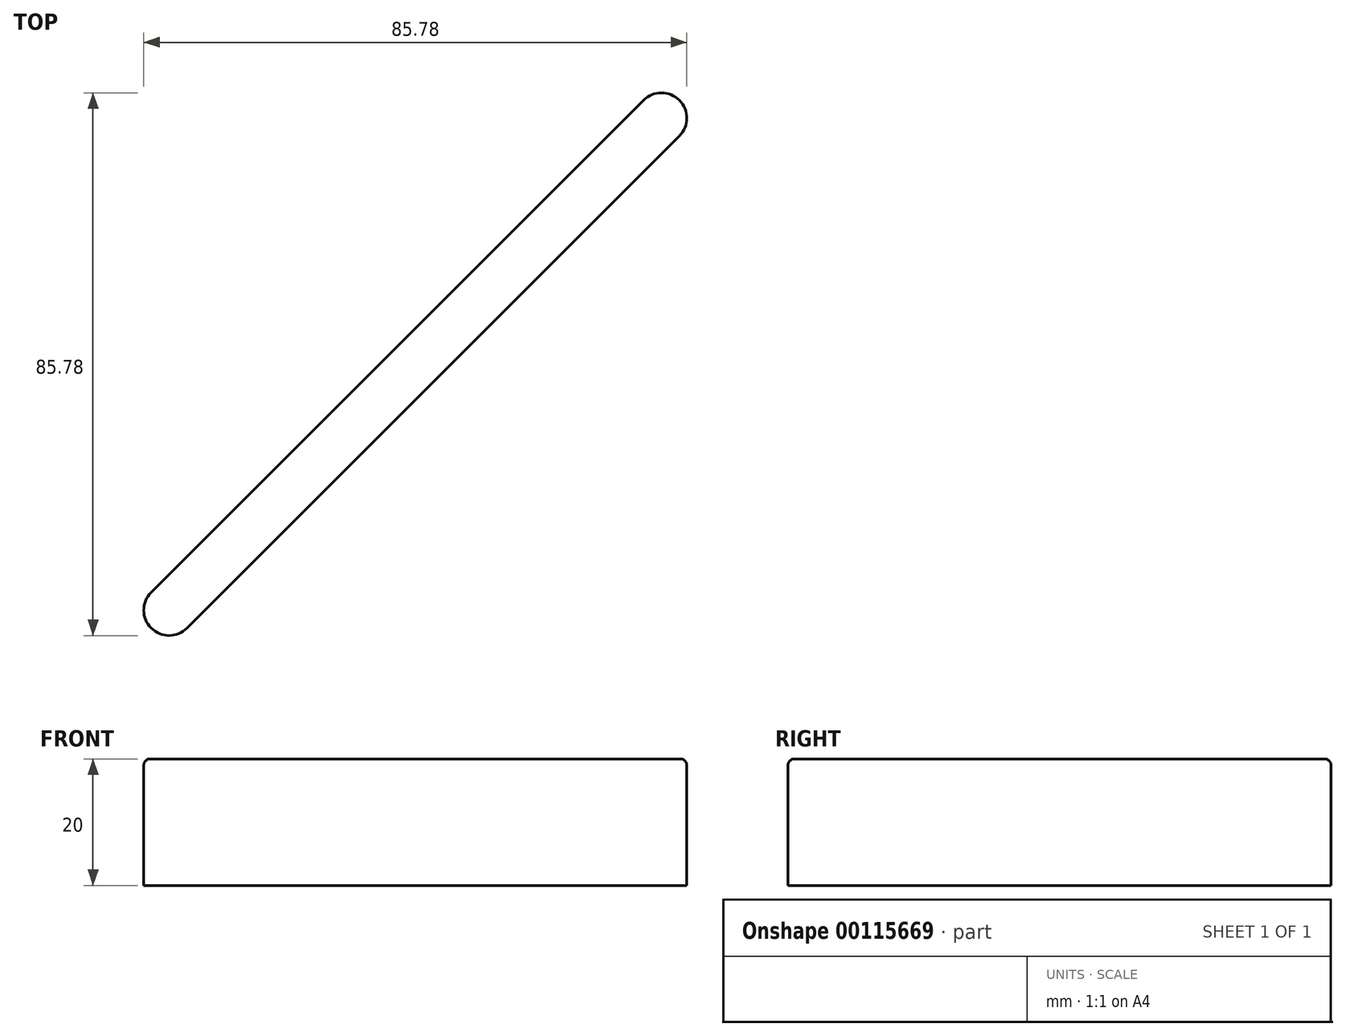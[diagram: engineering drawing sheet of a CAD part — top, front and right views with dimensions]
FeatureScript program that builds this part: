
annotation { "Feature Type Name" : "Feature", "Feature Type Description" : "" }
export const myFeature = defineFeature(function(context is Context, id is Id, definition is map)
    precondition{}
    {
        {
            var Q0;
            Q0=qCreatedBy(makeId("Top.planeOp"),FACE);
            var sketch = newSketch(context, id + "F0", { "sketchPlane" : qUnion([Q0])});
            skLineSegment(sketch, "E0.bottom", {"start": v(15.15, 65.55) * mm, "end": v(85.15, 65.55) * mm});
            skLineSegment(sketch, "E0.top", {"start": v(15.15, 58.55) * mm, "end": v(85.15, 58.55) * mm});
            skLineSegment(sketch, "E0.left", {"start": v(15.15, 65.55) * mm, "end": v(15.15, 58.55) * mm});
            skLineSegment(sketch, "E0.right", {"start": v(85.15, 65.55) * mm, "end": v(85.15, 58.55) * mm});
            skLineSegment(sketch, "E1", {"start": v(-34.78, -47.52) * mm, "end": v(71.3, 58.55) * mm});
            skLineSegment(sketch, "E2", {"start": v(71.3, 58.55) * mm, "end": v(43, 58.55) * mm});
            skLineSegment(sketch, "E3", {"start": v(43, 58.55) * mm, "end": v(-34.78, -19.23) * mm});
            skPoint(sketch, "E4", {"position": v(57.15, 58.55) * mm});
            skPoint(sketch, "E5", {"position": v(15.15, 58.55) * mm});
            skLineSegment(sketch, "E6", {"start": v(-34.78, -47.52) * mm, "end": v(-34.78, -19.23) * mm});
            skLineSegment(sketch, "E7", {"start": v(-34.78, 8.62) * mm, "end": v(-34.78, -61.38) * mm});
            skLineSegment(sketch, "E8", {"start": v(-34.78, -61.38) * mm, "end": v(-41.78, -61.38) * mm});
            skLineSegment(sketch, "E9", {"start": v(-34.78, 8.62) * mm, "end": v(-41.78, 8.62) * mm});
            skLineSegment(sketch, "E10", {"start": v(-41.78, -61.38) * mm, "end": v(-41.78, 8.62) * mm});
            skPoint(sketch, "E11", {"position": v(-34.78, -33.38) * mm});
            skLineSegment(sketch, "E12", {"start": v(-34.78, -19.23) * mm, "end": v(-20.63, -33.38) * mm, "construction": true});
            skLineSegment(sketch, "E13", {"start": v(43, 58.55) * mm, "end": v(57.15, 44.4) * mm, "construction": true});
            skPoint(sketch, "E14", {"position": v(50.08, 51.48) * mm});
            skPoint(sketch, "E15", {"position": v(-27.7, -26.3) * mm});
            skLineSegment(sketch, "E16", {"start": v(77.5, 78.9) * mm, "end": v(-73.08, -71.68) * mm, "construction": true});
            skSolve(sketch);
        }
        {
            var Q0;
            Q0=makeQuery(id+"F0.imprint","IMPRINT",FACE,{"disambiguationData":[TD([[makeQuery(id+"F0.imprint","IMPRINT",EDGE,{"derivedFrom":sQuery(id+"F0.wireOp",EDGE,"73e61f8d-8661-40f2-8c05-ec82681df63f.top")}),1.0]])]});
            var Q1;
            {var subQ0=sQuery(id+"F0.wireOp",EDGE,"E1");Q1=makeQuery(id+"F0.imprint","IMPRINT",FACE,{"disambiguationData":[TD([[makeQuery(id+"F0.imprint","IMPRINT",EDGE,{"derivedFrom":subQ0}),1.0]])]});}
            var Q2;
            Q2=makeQuery(id+"F0.imprint","IMPRINT",FACE,{"disambiguationData":[TD([[makeQuery(id+"F0.imprint","IMPRINT",EDGE,{"derivedFrom":sQuery(id+"F0.wireOp",EDGE,"E0.bottom")}),-1.0]])]});
            var Q3;
            {var subQ0=sQuery(id+"F0.wireOp",EDGE,"E8");Q3=makeQuery(id+"F0.imprint","IMPRINT",FACE,{"disambiguationData":[TD([[makeQuery(id+"F0.imprint","IMPRINT",EDGE,{"derivedFrom":subQ0}),-1.0]])]});}
            extrude(context, id + "F1", {"entities" : qUnion([Q0, Q1, Q2, Q3]), "oppositeDirection" : true, "depth" : 20 * mm});
        }
        {
            var Q0;
            {var subQ0=sQuery(id+"F0.wireOp",EDGE,"E0.top");Q0=makeQuery(id+"F1.opExtrude","SWEPT_FACE",FACE,{"disambiguationData":[OSD([subQ0]),TDD([makeQuery(id+"F0.imprint","IMPRINT",EDGE,{"disambiguationData":[TD([[makeQuery(id+"F0.imprint","INTERSECT",VERTEX,{"derivedFrom":[subQ0,sQuery(id+"F0.wireOp",EDGE,"E0.right")]}),1.0]])],"derivedFrom":subQ0})])]});}
            var sketch = newSketch(context, id + "F2", { "sketchPlane" : qUnion([Q0])});
            skPoint(sketch, "E17", {"position": v(78.22, 0) * mm});
            skPoint(sketch, "E18", {"position": v(85.15, -10) * mm});
            skPoint(sketch, "E19", {"position": v(78.22, -10) * mm});
            skSolve(sketch);
        }
        {
            var Q0;
            {var subQ0=sQuery(id+"F0.wireOp",EDGE,"E7");Q0=makeQuery(id+"F1.opExtrude","SWEPT_FACE",FACE,{"disambiguationData":[OSD([subQ0]),TDD([makeQuery(id+"F0.imprint","IMPRINT",EDGE,{"disambiguationData":[TD([[makeQuery(id+"F0.imprint","INTERSECT",VERTEX,{"derivedFrom":[sQuery(id+"F0.wireOp",EDGE,"E1"),subQ0]}),-1.0]])],"derivedFrom":subQ0})])]});}
            var sketch = newSketch(context, id + "F3", { "sketchPlane" : qUnion([Q0])});
            skPoint(sketch, "E20", {"position": v(-61.38, 0) * mm});
            skPoint(sketch, "E21", {"position": v(-54.45, 0) * mm});
            skPoint(sketch, "E22", {"position": v(-61.38, -10) * mm});
            skPoint(sketch, "E23", {"position": v(-54.45, -10) * mm});
            skSolve(sketch);
        }
        {
            var Q0;
            {var subQ0=sQuery(id+"F0.wireOp",EDGE,"E0.top");Q0=makeQuery(id+"F1.opExtrude","SWEPT_FACE",FACE,{"disambiguationData":[OSD([subQ0]),TDD([makeQuery(id+"F0.imprint","IMPRINT",EDGE,{"disambiguationData":[TD([[makeQuery(id+"F0.imprint","INTERSECT",VERTEX,{"derivedFrom":[subQ0,sQuery(id+"F0.wireOp",EDGE,"E0.left")]}),-1.0]])],"derivedFrom":subQ0})])]});}
            var sketch = newSketch(context, id + "F4", { "sketchPlane" : qUnion([Q0])});
            skPoint(sketch, "E24", {"position": v(15.15, -10) * mm});
            skPoint(sketch, "E25", {"position": v(22.08, 0) * mm});
            skPoint(sketch, "E26", {"position": v(22.08, -10) * mm});
            skSolve(sketch);
        }
        {
            var Q0;
            {var subQ0=sQuery(id+"F0.wireOp",EDGE,"E7");Q0=makeQuery(id+"F1.opExtrude","SWEPT_FACE",FACE,{"disambiguationData":[OSD([subQ0]),TDD([makeQuery(id+"F0.imprint","IMPRINT",EDGE,{"disambiguationData":[TD([[makeQuery(id+"F0.imprint","INTERSECT",VERTEX,{"derivedFrom":[sQuery(id+"F0.wireOp",EDGE,"E3"),subQ0]}),1.0]])],"derivedFrom":subQ0})])]});}
            var sketch = newSketch(context, id + "F5", { "sketchPlane" : qUnion([Q0])});
            skPoint(sketch, "E27", {"position": v(8.62, -20) * mm});
            skPoint(sketch, "E28", {"position": v(8.62, -10) * mm});
            skPoint(sketch, "E29", {"position": v(1.7, -20) * mm});
            skPoint(sketch, "E30", {"position": v(1.7, -10) * mm});
            skSolve(sketch);
        }
        {
            var Q0;
            Q0=sQuery(id+"F5.wireOp",VERTEX,"E30");
            var Q1;
            Q1=sQuery(id+"F3.wireOp",VERTEX,"E23");
            var Q2;
            Q2=sQuery(id+"F4.wireOp",VERTEX,"E26");
            var Q3;
            Q3=sQuery(id+"F2.wireOp",VERTEX,"E19");
            var Q4;
            Q4=makeQuery(id+"F1.opExtrude","SWEPT_BODY",BODY,{"disambiguationData":[OSD([sQuery(id+"F0.wireOp",EDGE,"E0.bottom"),sQuery(id+"F0.wireOp",EDGE,"E0.top"),sQuery(id+"F0.wireOp",EDGE,"E0.left"),sQuery(id+"F0.wireOp",EDGE,"E0.right"),sQuery(id+"F0.wireOp",EDGE,"E1"),sQuery(id+"F0.wireOp",EDGE,"E3"),sQuery(id+"F0.wireOp",EDGE,"E7"),sQuery(id+"F0.wireOp",EDGE,"E8"),sQuery(id+"F0.wireOp",EDGE,"E9"),sQuery(id+"F0.wireOp",EDGE,"E10")])]});
            hole(context, id + "F6", {"style" : HoleStyle.SIMPLE, "endStyle" : HoleEndStyle.THROUGH, "standardTappedOrClearance" : lookupTablePath({ "standard" : "ISO", "fit" : "Normal", "size" : "M5", "type" : "Clearance" }), "standardBlindInLast" : lookupTablePath({ "fit" : "Standard", "standard" : "ISO", "size" : "M5", "type" : "Clearance" }), "holeDiameter" : 5.5 * mm, "locations" : qUnion([Q0, Q1, Q2, Q3]), "scope" : qUnion([Q4]), "isTappedThrough" : true});
        }
        {
            var Q0;
            Q0=makeQuery(id+"F1.opExtrude","SWEPT_EDGE",EDGE,{"disambiguationData":[OSD([sQuery(id+"F0.wireOp",EDGE,"E1"),sQuery(id+"F0.wireOp",EDGE,"E7")])]});
            var Q1;
            Q1=makeQuery(id+"F1.opExtrude","SWEPT_EDGE",EDGE,{"disambiguationData":[OSD([sQuery(id+"F0.wireOp",EDGE,"E0.top"),sQuery(id+"F0.wireOp",EDGE,"E1"),sQuery(id+"F0.wireOp",EDGE,"E2")])]});
            fillet(context, id + "F7", {"entities" : qUnion([Q0, Q1]), "radius" : 5 * mm, "tangentPropagation" : true, "allowEdgeOverflow" : false});
        }
        {
            var Q0;
            Q0=makeQuery(id+"F1.opExtrude","SWEPT_EDGE",EDGE,{"disambiguationData":[OSD([sQuery(id+"F0.wireOp",EDGE,"E3"),sQuery(id+"F0.wireOp",EDGE,"E7")])]});
            var Q1;
            Q1=makeQuery(id+"F1.opExtrude","SWEPT_EDGE",EDGE,{"disambiguationData":[OSD([sQuery(id+"F0.wireOp",EDGE,"E0.top"),sQuery(id+"F0.wireOp",EDGE,"E2"),sQuery(id+"F0.wireOp",EDGE,"E3")])]});
            fillet(context, id + "F8", {"entities" : qUnion([Q0, Q1]), "radius" : 5 * mm, "tangentPropagation" : true, "allowEdgeOverflow" : false});
        }
        {
            var Q0;
            Q0=makeQuery(id+"F1.opExtrude","CAP_FACE",FACE,{"disambiguationData":[OSD([sQuery(id+"F0.wireOp",EDGE,"E0.bottom"),sQuery(id+"F0.wireOp",EDGE,"E0.top"),sQuery(id+"F0.wireOp",EDGE,"E0.left"),sQuery(id+"F0.wireOp",EDGE,"E0.right"),sQuery(id+"F0.wireOp",EDGE,"E1"),sQuery(id+"F0.wireOp",EDGE,"E3"),sQuery(id+"F0.wireOp",EDGE,"E7"),sQuery(id+"F0.wireOp",EDGE,"E8"),sQuery(id+"F0.wireOp",EDGE,"E9"),sQuery(id+"F0.wireOp",EDGE,"E10")])],"isStart":false});
            var sketch = newSketch(context, id + "F9", { "sketchPlane" : qUnion([Q0])});
            skLineSegment(sketch, "E31", {"start": v(50.08, -51.48) * mm, "end": v(-27.7, 26.3) * mm});
            skArc(sketch, "E32.0.startCap", {"start": v(52.9, -48.65) * mm, "mid": v(52.9, -54.3) * mm, "end": v(47.25, -54.3) * mm});
            skArc(sketch, "E32.0.endCap", {"start": v(-30.53, 23.48) * mm, "mid": v(-30.53, 29.13) * mm, "end": v(-24.88, 29.13) * mm});
            skLineSegment(sketch, "E32.0.left", {"start": v(47.25, -54.3) * mm, "end": v(-30.53, 23.48) * mm});
            skLineSegment(sketch, "E32.0.right", {"start": v(52.9, -48.65) * mm, "end": v(-24.88, 29.13) * mm});
            skSolve(sketch);
        }
        {
            var Q0;
            Q0=makeQuery(id+"F9.imprint","IMPRINT",FACE,{"disambiguationData":[TD([[makeQuery(id+"F9.imprint","IMPRINT",EDGE,{"derivedFrom":sQuery(id+"F9.wireOp",EDGE,"E32.0.startCap")}),-1.0]])]});
            extrude(context, id + "F10", {"entities" : qUnion([Q0]), "operationType" : NewBodyOperationType.REMOVE, "endBound" : BoundingType.THROUGH_ALL, "oppositeDirection" : true, "depth" : 25 * mm});
        }
        {
            var Q0;
            Q0=makeQuery(id+"F1.opExtrude","SWEPT_EDGE",EDGE,{"disambiguationData":[OSD([sQuery(id+"F0.wireOp",EDGE,"E0.top"),sQuery(id+"F0.wireOp",EDGE,"E0.right")])]});
            var Q1;
            Q1=makeQuery(id+"F1.opExtrude","SWEPT_EDGE",EDGE,{"disambiguationData":[OSD([sQuery(id+"F0.wireOp",EDGE,"E0.top"),sQuery(id+"F0.wireOp",EDGE,"E0.left")])]});
            var Q2;
            Q2=makeQuery(id+"F1.opExtrude","SWEPT_EDGE",EDGE,{"disambiguationData":[OSD([sQuery(id+"F0.wireOp",EDGE,"E7"),sQuery(id+"F0.wireOp",EDGE,"E9")])]});
            var Q3;
            Q3=makeQuery(id+"F1.opExtrude","SWEPT_EDGE",EDGE,{"disambiguationData":[OSD([sQuery(id+"F0.wireOp",EDGE,"E7"),sQuery(id+"F0.wireOp",EDGE,"E8")])]});
            var Q4;
            Q4=makeQuery(id+"F10.boolean.opBoolean","COPY",EDGE,{"derivedFrom":makeQuery(id+"F10.opExtrude","CAP_EDGE",EDGE,{"disambiguationData":[OSD([sQuery(id+"F9.wireOp",EDGE,"E32.0.right")])],"isStart":true})});
            var Q5;
            Q5=makeQuery(id+"F10.boolean.opBoolean","INTERSECT",EDGE,{"derivedFrom":[makeQuery(id+"F1.opExtrude","CAP_FACE",FACE,{"disambiguationData":[OSD([sQuery(id+"F0.wireOp",EDGE,"E0.bottom"),sQuery(id+"F0.wireOp",EDGE,"E0.top"),sQuery(id+"F0.wireOp",EDGE,"E0.left"),sQuery(id+"F0.wireOp",EDGE,"E0.right"),sQuery(id+"F0.wireOp",EDGE,"E1"),sQuery(id+"F0.wireOp",EDGE,"E3"),sQuery(id+"F0.wireOp",EDGE,"E7"),sQuery(id+"F0.wireOp",EDGE,"E8"),sQuery(id+"F0.wireOp",EDGE,"E9"),sQuery(id+"F0.wireOp",EDGE,"E10")])],"isStart":true}),makeQuery(id+"F10.opExtrude","SWEPT_FACE",FACE,{"disambiguationData":[OSD([sQuery(id+"F9.wireOp",EDGE,"E32.0.left")])]})]});
            var Q6;
            {var subQ0=sQuery(id+"F0.wireOp",EDGE,"E7");Q6=makeQuery(id+"F1.opExtrude","CAP_EDGE",EDGE,{"disambiguationData":[OSD([subQ0]),TDD([makeQuery(id+"F0.imprint","IMPRINT",EDGE,{"disambiguationData":[TD([[makeQuery(id+"F0.imprint","INTERSECT",VERTEX,{"derivedFrom":[sQuery(id+"F0.wireOp",EDGE,"E3"),subQ0]}),1.0]])],"derivedFrom":subQ0})])],"isStart":true});}
            var Q7;
            {var subQ0=sQuery(id+"F0.wireOp",EDGE,"E7");Q7=makeQuery(id+"F1.opExtrude","CAP_EDGE",EDGE,{"disambiguationData":[OSD([subQ0]),TDD([makeQuery(id+"F0.imprint","IMPRINT",EDGE,{"disambiguationData":[TD([[makeQuery(id+"F0.imprint","INTERSECT",VERTEX,{"derivedFrom":[sQuery(id+"F0.wireOp",EDGE,"E3"),subQ0]}),1.0]])],"derivedFrom":subQ0})])],"isStart":false});}
            var Q8;
            {var subQ0=sQuery(id+"F0.wireOp",EDGE,"E7");Q8=makeQuery(id+"F1.opExtrude","CAP_EDGE",EDGE,{"disambiguationData":[OSD([subQ0]),TDD([makeQuery(id+"F0.imprint","IMPRINT",EDGE,{"disambiguationData":[TD([[makeQuery(id+"F0.imprint","INTERSECT",VERTEX,{"derivedFrom":[sQuery(id+"F0.wireOp",EDGE,"E1"),subQ0]}),-1.0]])],"derivedFrom":subQ0})])],"isStart":true});}
            var Q9;
            {var subQ0=sQuery(id+"F0.wireOp",EDGE,"E7");Q9=makeQuery(id+"F1.opExtrude","CAP_EDGE",EDGE,{"disambiguationData":[OSD([subQ0]),TDD([makeQuery(id+"F0.imprint","IMPRINT",EDGE,{"disambiguationData":[TD([[makeQuery(id+"F0.imprint","INTERSECT",VERTEX,{"derivedFrom":[sQuery(id+"F0.wireOp",EDGE,"E1"),subQ0]}),-1.0]])],"derivedFrom":subQ0})])],"isStart":false});}
            var Q10;
            Q10=makeQuery(id+"F1.opExtrude","CAP_EDGE",EDGE,{"disambiguationData":[OSD([sQuery(id+"F0.wireOp",EDGE,"E8")])],"isStart":false});
            var Q11;
            Q11=makeQuery(id+"F1.opExtrude","CAP_EDGE",EDGE,{"disambiguationData":[OSD([sQuery(id+"F0.wireOp",EDGE,"E9")])],"isStart":false});
            var Q12;
            Q12=makeQuery(id+"F1.opExtrude","CAP_EDGE",EDGE,{"disambiguationData":[OSD([sQuery(id+"F0.wireOp",EDGE,"E9")])],"isStart":true});
            var Q13;
            Q13=makeQuery(id+"F1.opExtrude","CAP_EDGE",EDGE,{"disambiguationData":[OSD([sQuery(id+"F0.wireOp",EDGE,"E0.left")])],"isStart":false});
            var Q14;
            Q14=makeQuery(id+"F1.opExtrude","CAP_EDGE",EDGE,{"disambiguationData":[OSD([sQuery(id+"F0.wireOp",EDGE,"E0.right")])],"isStart":false});
            var Q15;
            Q15=makeQuery(id+"F1.opExtrude","CAP_EDGE",EDGE,{"disambiguationData":[OSD([sQuery(id+"F0.wireOp",EDGE,"E0.right")])],"isStart":true});
            var Q16;
            Q16=makeQuery(id+"F1.opExtrude","CAP_EDGE",EDGE,{"disambiguationData":[OSD([sQuery(id+"F0.wireOp",EDGE,"E0.left")])],"isStart":true});
            var Q17;
            Q17=makeQuery(id+"F1.opExtrude","CAP_EDGE",EDGE,{"disambiguationData":[OSD([sQuery(id+"F0.wireOp",EDGE,"E8")])],"isStart":true});
            fillet(context, id + "F11", {"entities" : qUnion([Q0, Q1, Q2, Q3, Q4, Q5, Q6, Q7, Q8, Q9, Q10, Q11, Q12, Q13, Q14, Q15, Q16, Q17]), "radius" : 1 * mm, "tangentPropagation" : true, "allowEdgeOverflow" : false});
        }
    });
